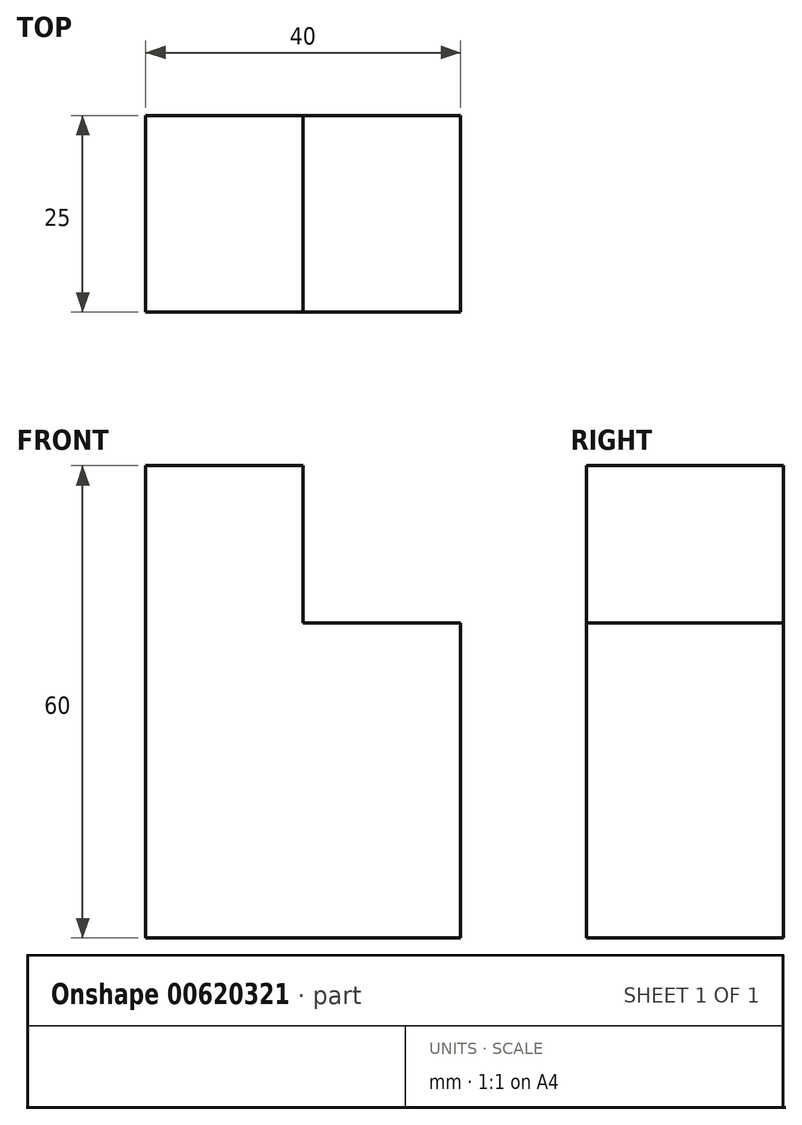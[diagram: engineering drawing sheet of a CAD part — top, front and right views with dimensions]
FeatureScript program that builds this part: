
annotation { "Feature Type Name" : "Feature", "Feature Type Description" : "" }
export const myFeature = defineFeature(function(context is Context, id is Id, definition is map)
    precondition{}
    {
        {
            var Q0;
            Q0=qCreatedBy(makeId("Front.planeOp"),FACE);
            var sketch = newSketch(context, id + "F0", { "sketchPlane" : qUnion([Q0])});
            skLineSegment(sketch, "E0", {"start": v(-62.25, 45.6) * mm, "end": v(-62.25, -14.4) * mm});
            skLineSegment(sketch, "E1", {"start": v(-62.25, -14.4) * mm, "end": v(-22.25, -14.4) * mm});
            skLineSegment(sketch, "E2", {"start": v(-22.25, -14.4) * mm, "end": v(-22.25, 25.6) * mm});
            skLineSegment(sketch, "E3", {"start": v(-22.25, 25.6) * mm, "end": v(-62.25, 25.6) * mm});
            skLineSegment(sketch, "E4", {"start": v(-62.25, 45.6) * mm, "end": v(-42.25, 45.6) * mm});
            skLineSegment(sketch, "E5", {"start": v(-42.25, 45.6) * mm, "end": v(-42.25, 25.6) * mm});
            skSolve(sketch);
        }
        {
            var Q0;
            Q0 = qSketchRegion(id + "F0", true);
            extrude(context, id + "F1", {"entities" : qUnion([Q0]), "depth" : 25 * mm, "offsetDistance" : 25 * mm});
        }
    });
